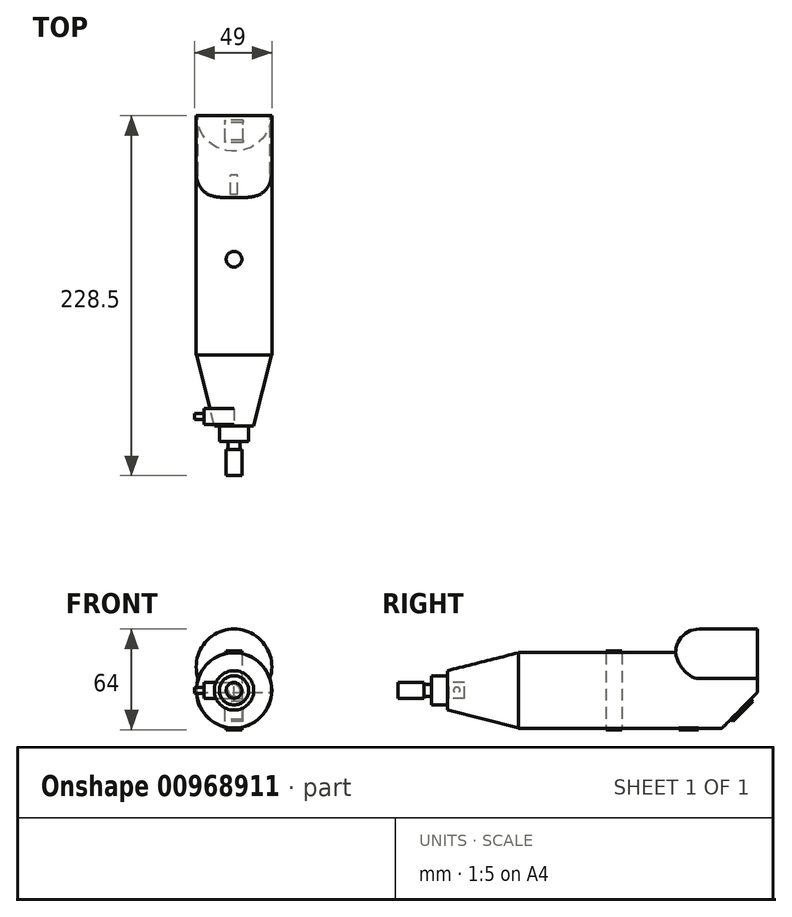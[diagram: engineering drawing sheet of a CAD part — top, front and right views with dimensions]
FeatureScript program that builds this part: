
annotation { "Feature Type Name" : "Feature", "Feature Type Description" : "" }
export const myFeature = defineFeature(function(context is Context, id is Id, definition is map)
    precondition{}
    {
        {
            var Q0;
            Q0=qCreatedBy(makeId("Front.planeOp"),FACE);
            var sketch = newSketch(context, id + "F0", { "sketchPlane" : qUnion([Q0])});
            skCircle(sketch, "E0", {"center": v(0, 0) * mm, "radius": 24 * mm});
            skSolve(sketch);
        }
        {
            var Q0;
            Q0=makeQuery(id+"F0.imprint","IMPRINT",FACE,{"disambiguationData":[TD([[makeQuery(id+"F0.imprint","IMPRINT",EDGE,{"derivedFrom":sQuery(id+"F0.wireOp",EDGE,"E0")}),1.0]])]});
            extrude(context, id + "F1", {"entities" : qUnion([Q0]), "depth" : 152 * mm, "offsetDistance" : 25 * mm});
        }
        {
            var Q0;
            Q0=qCreatedBy(makeId("Front.planeOp"),FACE);
            var sketch = newSketch(context, id + "F2", { "sketchPlane" : qUnion([Q0])});
            skCircle(sketch, "E1", {"center": v(0, 15) * mm, "radius": 24 * mm});
            skSolve(sketch);
        }
        {
            var Q0;
            Q0 = qSketchRegion(id + "F2", true);
            extrude(context, id + "F3", {"entities" : qUnion([Q0]), "operationType" : NewBodyOperationType.ADD, "depth" : 52 * mm, "offsetDistance" : 25 * mm});
        }
        {
            var Q0;
            Q0=qCreatedBy(makeId("Right.planeOp"),FACE);
            var sketch = newSketch(context, id + "F4", { "sketchPlane" : qUnion([Q0])});
            skLineSegment(sketch, "E2", {"start": v(-152, 0) * mm, "end": v(-197, 0) * mm});
            skLineSegment(sketch, "E3", {"start": v(-197, 0) * mm, "end": v(-197, 12.5) * mm});
            skLineSegment(sketch, "E4", {"start": v(-197, 12.5) * mm, "end": v(-151.57, 24) * mm});
            skLineSegment(sketch, "E5", {"start": v(-151.57, 24) * mm, "end": v(-152, 0) * mm});
            skSolve(sketch);
        }
        {
            var Q0;
            Q0=makeQuery(id+"F4.imprint","IMPRINT",FACE,{"disambiguationData":[TD([[makeQuery(id+"F4.imprint","IMPRINT",EDGE,{"derivedFrom":sQuery(id+"F4.wireOp",EDGE,"E2")}),-1.0]])]});
            var Q1;
            Q1=sQuery(id+"F4.wireOp",EDGE,"E2");
            revolve(context, id + "F5", {"operationType" : NewBodyOperationType.ADD, "surfaceOperationType" : NewSurfaceOperationType.NEW, "entities" : qUnion([Q0]), "axis" : qUnion([Q1]), "revolveType" : RevolveType.FULL});
        }
        {
            var Q0;
            Q0=qCreatedBy(makeId("Right.planeOp"),FACE);
            var sketch = newSketch(context, id + "F6", { "sketchPlane" : qUnion([Q0])});
            skLineSegment(sketch, "E6", {"start": v(-197, 0) * mm, "end": v(-207, 0) * mm});
            skLineSegment(sketch, "E7", {"start": v(-207, 0) * mm, "end": v(-207, 9.25) * mm});
            skLineSegment(sketch, "E8", {"start": v(-207, 9.25) * mm, "end": v(-197, 9.25) * mm});
            skLineSegment(sketch, "E9", {"start": v(-197, 9.25) * mm, "end": v(-197, 0) * mm});
            skSolve(sketch);
        }
        {
            var Q0;
            Q0 = qSketchRegion(id + "F6", true);
            var Q1;
            Q1=sQuery(id+"F6.wireOp",EDGE,"E6");
            revolve(context, id + "F7", {"operationType" : NewBodyOperationType.ADD, "surfaceOperationType" : NewSurfaceOperationType.NEW, "entities" : qUnion([Q0]), "axis" : qUnion([Q1]), "revolveType" : RevolveType.FULL});
        }
        {
            var Q0;
            Q0=qCreatedBy(makeId("Right.planeOp"),FACE);
            var sketch = newSketch(context, id + "F8", { "sketchPlane" : qUnion([Q0])});
            skLineSegment(sketch, "E10", {"start": v(-207, 0) * mm, "end": v(-228.5, 0) * mm});
            skLineSegment(sketch, "E11", {"start": v(-228.5, 0) * mm, "end": v(-228.5, 5) * mm});
            skLineSegment(sketch, "E12", {"start": v(-207, 0) * mm, "end": v(-207, 3.75) * mm});
            skLineSegment(sketch, "E13", {"start": v(-207, 3.75) * mm, "end": v(-212, 3.75) * mm});
            skLineSegment(sketch, "E14", {"start": v(-212, 3.75) * mm, "end": v(-212, 5) * mm});
            skLineSegment(sketch, "E15", {"start": v(-212, 5) * mm, "end": v(-228.5, 5) * mm});
            skSolve(sketch);
        }
        {
            var Q0;
            Q0 = qSketchRegion(id + "F8", true);
            var Q1;
            Q1=sQuery(id+"F8.wireOp",EDGE,"E10");
            revolve(context, id + "F9", {"operationType" : NewBodyOperationType.ADD, "surfaceOperationType" : NewSurfaceOperationType.NEW, "entities" : qUnion([Q0]), "axis" : qUnion([Q1]), "revolveType" : RevolveType.FULL});
        }
        {
            var Q0;
            Q0=qCreatedBy(makeId("Top.planeOp"),FACE);
            var sketch = newSketch(context, id + "F10", { "sketchPlane" : qUnion([Q0])});
            skLineSegment(sketch, "E16.bottom", {"start": v(5, -186) * mm, "end": v(-5, -186) * mm});
            skLineSegment(sketch, "E16.top", {"start": v(5, -196) * mm, "end": v(-5, -196) * mm});
            skLineSegment(sketch, "E16.left", {"start": v(5, -186) * mm, "end": v(5, -196) * mm});
            skLineSegment(sketch, "E16.right", {"start": v(-5, -186) * mm, "end": v(-5, -196) * mm});
            skPoint(sketch, "E16.middle", {"position": v(0, -191) * mm});
            skSolve(sketch);
        }
        {
            var Q0;
            Q0 = qSketchRegion(id + "F10", true);
            extrude(context, id + "F11", {"entities" : qUnion([Q0]), "depth" : -19 * mm, "offsetDistance" : 25 * mm});
        }
        {
            var Q0;
            Q0=makeQuery(id+"F11.opExtrude","CAP_FACE",FACE,{"disambiguationData":[OSD([sQuery(id+"F10.wireOp",EDGE,"E16.bottom"),sQuery(id+"F10.wireOp",EDGE,"E16.top"),sQuery(id+"F10.wireOp",EDGE,"E16.left"),sQuery(id+"F10.wireOp",EDGE,"E16.right")])],"isStart":false});
            var sketch = newSketch(context, id + "F12", { "sketchPlane" : qUnion([Q0])});
            skCircle(sketch, "E17", {"center": v(0, 191) * mm, "radius": 2 * mm});
            skPoint(sketch, "E17.centerSnap0", {"position": v(5, 191) * mm});
            skSolve(sketch);
        }
        {
            var Q0;
            Q0=makeQuery(id+"F12.imprint","IMPRINT",FACE,{"disambiguationData":[TD([[makeQuery(id+"F12.imprint","IMPRINT",EDGE,{"derivedFrom":sQuery(id+"F12.wireOp",EDGE,"E17")}),1.0]])]});
            extrude(context, id + "F13", {"entities" : qUnion([Q0]), "depth" : 6 * mm, "offsetDistance" : 25 * mm});
        }
        {
            var Q0;
            Q0=qCreatedBy(makeId("Right.planeOp"),FACE);
            var sketch = newSketch(context, id + "F14", { "sketchPlane" : qUnion([Q0])});
            skLineSegment(sketch, "E18", {"start": v(0, -24.33) * mm, "end": v(-23, -24.33) * mm});
            skLineSegment(sketch, "E19", {"start": v(-23, -24.33) * mm, "end": v(0, -1.33) * mm});
            skLineSegment(sketch, "E20", {"start": v(0, -1.33) * mm, "end": v(0, -24.33) * mm});
            skSolve(sketch);
        }
        {
            var Q0;
            Q0=makeQuery(id+"F14.imprint","IMPRINT",FACE,{"disambiguationData":[TD([[makeQuery(id+"F14.imprint","IMPRINT",EDGE,{"derivedFrom":sQuery(id+"F14.wireOp",EDGE,"E18")}),-1.0]])]});
            extrude(context, id + "F15", {"entities" : qUnion([Q0]), "operationType" : NewBodyOperationType.REMOVE, "endBound" : BoundingType.SYMMETRIC, "oppositeDirection" : true, "depth" : 60 * mm, "offsetDistance" : 25 * mm});
        }
        {
            var Q0;
            Q0=makeQuery(id+"F15.boolean.opBoolean","COPY",FACE,{"derivedFrom":makeQuery(id+"F15.opExtrude","SWEPT_FACE",FACE,{"disambiguationData":[OSD([sQuery(id+"F14.wireOp",EDGE,"E19")])]})});
            var sketch = newSketch(context, id + "F16", { "sketchPlane" : qUnion([Q0])});
            skLineSegment(sketch, "E21.bottom", {"start": v(-5.73, -24.98) * mm, "end": v(5.73, -24.98) * mm});
            skLineSegment(sketch, "E21.top", {"start": v(-5.73, -6.87) * mm, "end": v(5.73, -6.87) * mm});
            skLineSegment(sketch, "E21.left", {"start": v(-5.73, -24.98) * mm, "end": v(-5.73, -6.87) * mm});
            skLineSegment(sketch, "E21.right", {"start": v(5.73, -24.98) * mm, "end": v(5.73, -6.87) * mm});
            skPoint(sketch, "E21.middle", {"position": v(0, -15.92) * mm});
            skSolve(sketch);
        }
        {
            var Q0;
            Q0=makeQuery(id+"F16.imprint","IMPRINT",FACE,{"disambiguationData":[TD([[makeQuery(id+"F16.imprint","IMPRINT",EDGE,{"derivedFrom":sQuery(id+"F16.wireOp",EDGE,"E21.bottom")}),1.0]])]});
            extrude(context, id + "F17", {"entities" : qUnion([Q0]), "depth" : 2 * mm, "offsetDistance" : 25 * mm});
        }
        {
            var Q0;
            Q0=makeQuery(id+"F11.opExtrude","SWEPT_BODY",BODY,{"disambiguationData":[OSD([sQuery(id+"F10.wireOp",EDGE,"E16.bottom"),sQuery(id+"F10.wireOp",EDGE,"E16.top"),sQuery(id+"F10.wireOp",EDGE,"E16.left"),sQuery(id+"F10.wireOp",EDGE,"E16.right")])]});
            var Q1;
            Q1=makeQuery(id+"F13.opExtrude","SWEPT_BODY",BODY,{"disambiguationData":[OSD([sQuery(id+"F12.wireOp",EDGE,"E17")])]});
            var Q2;
            Q2=makeQuery(id+"F1.opExtrude","SWEPT_FACE",FACE,{"disambiguationData":[OSD([sQuery(id+"F0.wireOp",EDGE,"E0")])]});
            transform(context, id + "F18", {"entities" : qUnion([Q0, Q1]), "transformType" : TransformType.ROTATION, "transformAxis" : qUnion([Q2]), "angle" : 90 * degree, "makeCopy" : false});
        }
        {
            var Q0;
            Q0=qCreatedBy(makeId("Top.planeOp"),FACE);
            var sketch = newSketch(context, id + "F19", { "sketchPlane" : qUnion([Q0])});
            skCircle(sketch, "E22", {"center": v(0, -91.12) * mm, "radius": 5 * mm});
            skSolve(sketch);
        }
        {
            var Q0;
            Q0 = qSketchRegion(id + "F19", true);
            extrude(context, id + "F20", {"entities" : qUnion([Q0]), "endBound" : BoundingType.SYMMETRIC, "depth" : 50 * mm, "offsetDistance" : 25 * mm});
        }
        {
            var Q0;
            Q0=qCreatedBy(makeId("Top.planeOp"),FACE);
            var sketch = newSketch(context, id + "F21", { "sketchPlane" : qUnion([Q0])});
            skLineSegment(sketch, "E23.bottom", {"start": v(2.16, -37.64) * mm, "end": v(-2.16, -37.64) * mm});
            skLineSegment(sketch, "E23.top", {"start": v(2.16, -50) * mm, "end": v(-2.16, -50) * mm});
            skLineSegment(sketch, "E23.left", {"start": v(2.16, -37.64) * mm, "end": v(2.16, -50) * mm});
            skLineSegment(sketch, "E23.right", {"start": v(-2.16, -37.64) * mm, "end": v(-2.16, -50) * mm});
            skPoint(sketch, "E23.middle", {"position": v(0, -43.82) * mm});
            skSolve(sketch);
        }
        {
            var Q0;
            Q0 = qSketchRegion(id + "F21", true);
            extrude(context, id + "F22", {"entities" : qUnion([Q0]), "operationType" : NewBodyOperationType.ADD, "oppositeDirection" : true, "depth" : 25 * mm, "offsetDistance" : 25 * mm});
        }
        {
            var Q0;
            Q0=makeQuery(id+"F3.opExtrude","CAP_EDGE",EDGE,{"disambiguationData":[OSD([sQuery(id+"F2.wireOp",EDGE,"E1")])],"isStart":false});
            fillet(context, id + "F23", {"entities" : qUnion([Q0]), "radius" : 15 * mm, "tangentPropagation" : true, "allowEdgeOverflow" : false});
        }
    });
